# Revit family: 2059096 Lighting Fixture_Sylvania_Ascent 100 Arch(120)- Very High Output_Ceiling Recessed
name_source: partatom
category: Lighting Fixtures
revit_build: Autodesk Revit 2017 (Build: 20190507_1515(x64)
units: mm (PartAtom-declared; Revit-internal decimal feet)

## family parameters
Cut with Voids When Loaded = No
Host = Face
Light Source = Yes
OmniClass Number = 23.80.70.11.17
OmniClass Title = Specialized Lighting by Location or Use
Part Type = Normal
Room Calculation Point = No
Round Connector Dimension = Use Diameter
Shared = No

## types (1)
- Ascent100 Arch VHO 4K DALI 120
    Accessory Material = Aluminum_Sylvania_Ascent_White
    Aperture = 120 mm
    Apparent Load = 13 VA
    Assembly Code = D5020200
    Body Material = Aluminum_Sylvania_Ascent_White
    Catalog Number = 2059096 Ascent100 Arch VHO 4K DALI 120
    Color Filter = 16777215
    Cutout Diameter = 137 mm  [stored 0.449475 ft]
    Default Elevation = 0 mm  [stored 0 ft]
    Description = Direct LED retro fit for original LED 100 Arch (120) single CFL lamp offering Matching lumen levels and improved light distribution of original LED 100 CFL lamp equivalents Typically half the power consumption compared to CFL Up to 104lm/W 120mm aperture Architectural reflector accepts range of glass accessories from existing LED 100 Arch 120 offering HE, HO and VHO versions equivalent of single 1 x 13W, 1 x 18W, 1 x 26W Additional VVHO versions which offer the performance circa 2 x 26W equivalent
    Diameter = 150 mm
    Diffuser Material = Polycarbonate_Sylvania_Ascent_Clear
    Diffuser Radius = 53 mm  [stored 0.173885 ft]
    Dimming Lamp Color Temperature Shift = <None>
    Drive Current = 700mA
    Emit Shape Visible in Rendering = No
    Emit from Circle Diameter = 106 mm  [stored 0.347769 ft]
    Glow Wire Test = 850 °C
    Height = 94 mm  [stored 0.308399 ft]
    IK Rating = IK02
    IP Rating = IP44
    Lamp = Integrated LED
    Life = 50 000h
    Manufacturer = Feilo-Sylvania Group
    Model = Ascent100 Arch VHO 4K DALI 120
    Photometric Web File = 2059096_Ascent100ArchVHO4KDALI120-188541.ies
    Product Family = Ascent 100 Arch (120) - Very High Output
    Product Page URL = https://www.sylvania-lighting.com
    Radius = 75 mm
    Reflector Material = Aluminium_Sylvania_Ascent_Silver
    Reflector Radius = 60 mm  [stored 0.19685 ft]
    Tilt Angle = -90°
    URL = https://www.sylvania-lighting.com
    Voltage = 240 V
    Voltage Comments = UNV (Universal Voltage; 220-240 Volt)

note: [stored X ft] marks values corroborated as IEEE doubles in the binary element streams (Revit-internal decimal feet)

## geometry (parser evidence)
native form markers: Sweep x3
no freeform markers — native parametric forms only
